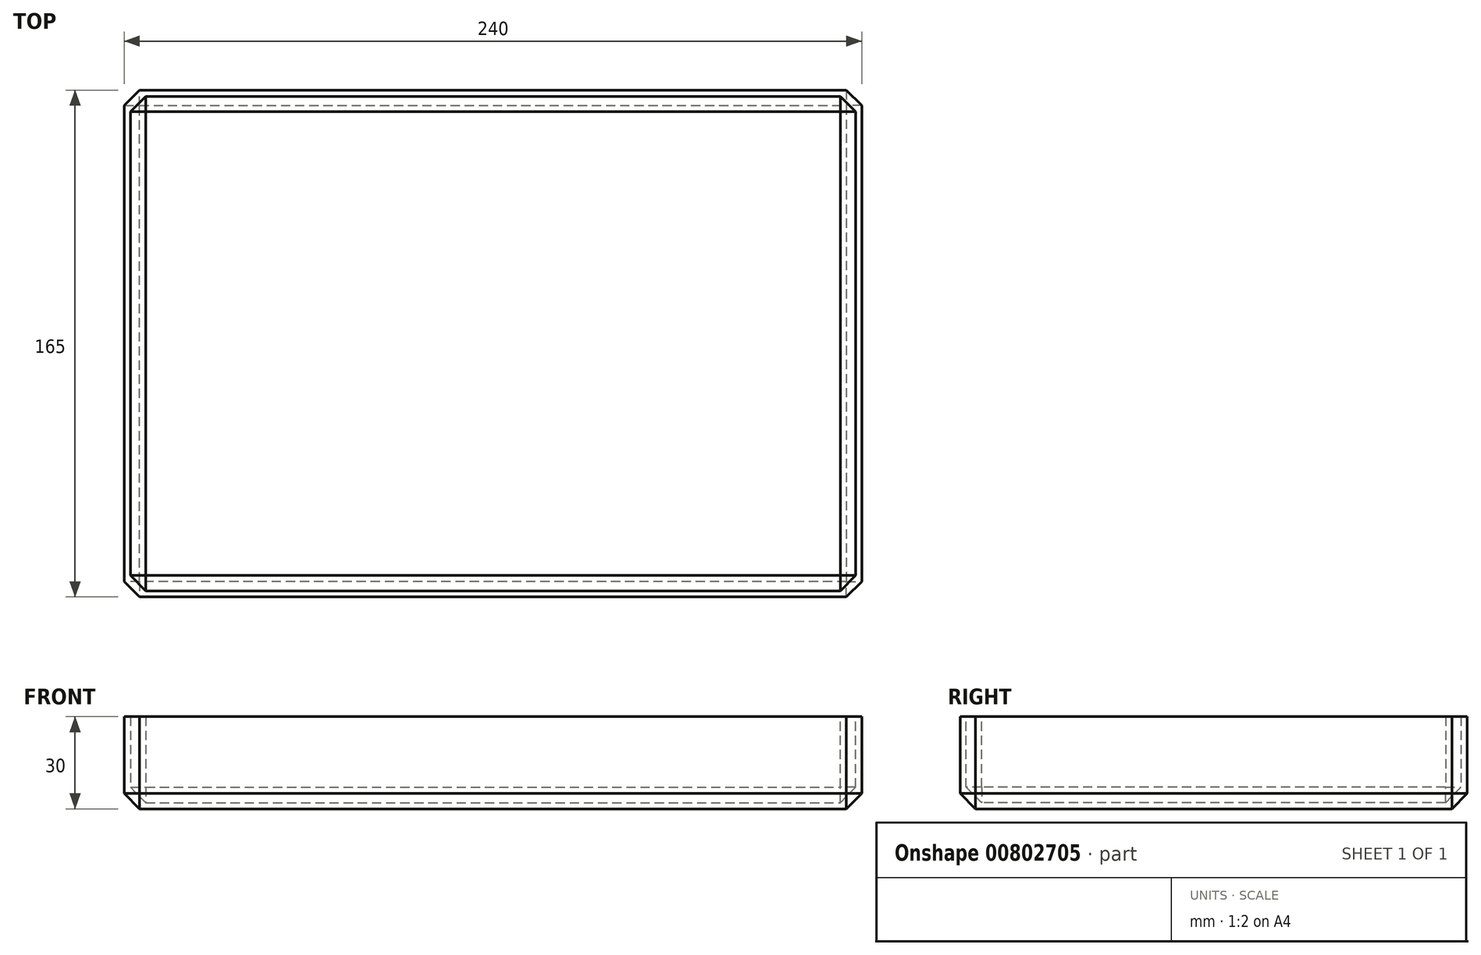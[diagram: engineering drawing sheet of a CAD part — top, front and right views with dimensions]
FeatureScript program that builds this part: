
annotation { "Feature Type Name" : "Feature", "Feature Type Description" : "" }
export const myFeature = defineFeature(function(context is Context, id is Id, definition is map)
    precondition{}
    {
        {
            var Q0;
            Q0=qCreatedBy(makeId("Top.planeOp"),FACE);
            var sketch = newSketch(context, id + "F0", { "sketchPlane" : qUnion([Q0])});
            skLineSegment(sketch, "E0.bottom", {"start": v(120, 82.5) * mm, "end": v(-120, 82.5) * mm});
            skLineSegment(sketch, "E0.top", {"start": v(120, -82.5) * mm, "end": v(-120, -82.5) * mm});
            skLineSegment(sketch, "E0.left", {"start": v(120, 82.5) * mm, "end": v(120, -82.5) * mm});
            skLineSegment(sketch, "E0.right", {"start": v(-120, 82.5) * mm, "end": v(-120, -82.5) * mm});
            skPoint(sketch, "E0.middle", {"position": v(0, 0) * mm});
            skSolve(sketch);
        }
        {
            var Q0;
            Q0 = qSketchRegion(id + "F0", true);
            extrude(context, id + "F1", {"entities" : qUnion([Q0]), "depth" : 30 * mm, "offsetDistance" : 25 * mm});
        }
        {
            var Q0;
            Q0=makeQuery(id+"F1.opExtrude","CAP_FACE",FACE,{"disambiguationData":[OSD([sQuery(id+"F0.wireOp",EDGE,"E0.bottom"),sQuery(id+"F0.wireOp",EDGE,"E0.top"),sQuery(id+"F0.wireOp",EDGE,"E0.left"),sQuery(id+"F0.wireOp",EDGE,"E0.right")])],"isStart":false});
            shell(context, id + "F2", {"entities" : qUnion([Q0]), "thickness" : 2 * mm});
        }
        {
            var Q0;
            Q0=makeQuery(id+"F2.opShell","OFFSET_EDGE",EDGE,{"disambiguationData":[OSD([sQuery(id+"F0.wireOp",EDGE,"E0.bottom"),sQuery(id+"F0.wireOp",EDGE,"E0.right")])]});
            var Q1;
            Q1=makeQuery(id+"F2.opShell","OFFSET_EDGE",EDGE,{"disambiguationData":[OSD([sQuery(id+"F0.wireOp",EDGE,"E0.bottom"),sQuery(id+"F0.wireOp",EDGE,"E0.left")])]});
            var Q2;
            Q2=makeQuery(id+"F2.opShell","OFFSET_EDGE",EDGE,{"disambiguationData":[OSD([sQuery(id+"F0.wireOp",EDGE,"E0.top"),sQuery(id+"F0.wireOp",EDGE,"E0.right")])]});
            var Q3;
            Q3=makeQuery(id+"F2.opShell","OFFSET_EDGE",EDGE,{"disambiguationData":[OSD([sQuery(id+"F0.wireOp",EDGE,"E0.top"),sQuery(id+"F0.wireOp",EDGE,"E0.left")])]});
            var Q4;
            Q4=makeQuery(id+"F1.opExtrude","SWEPT_EDGE",EDGE,{"disambiguationData":[OSD([sQuery(id+"F0.wireOp",EDGE,"E0.top"),sQuery(id+"F0.wireOp",EDGE,"E0.left")])]});
            var Q5;
            Q5=makeQuery(id+"F1.opExtrude","SWEPT_EDGE",EDGE,{"disambiguationData":[OSD([sQuery(id+"F0.wireOp",EDGE,"E0.bottom"),sQuery(id+"F0.wireOp",EDGE,"E0.left")])]});
            var Q6;
            Q6=makeQuery(id+"F1.opExtrude","SWEPT_EDGE",EDGE,{"disambiguationData":[OSD([sQuery(id+"F0.wireOp",EDGE,"E0.top"),sQuery(id+"F0.wireOp",EDGE,"E0.right")])]});
            var Q7;
            Q7=makeQuery(id+"F1.opExtrude","SWEPT_EDGE",EDGE,{"disambiguationData":[OSD([sQuery(id+"F0.wireOp",EDGE,"E0.bottom"),sQuery(id+"F0.wireOp",EDGE,"E0.right")])]});
            var Q8;
            Q8=makeQuery(id+"F1.opExtrude","CAP_FACE",FACE,{"disambiguationData":[OSD([sQuery(id+"F0.wireOp",EDGE,"E0.bottom"),sQuery(id+"F0.wireOp",EDGE,"E0.top"),sQuery(id+"F0.wireOp",EDGE,"E0.left"),sQuery(id+"F0.wireOp",EDGE,"E0.right")])],"isStart":true});
            var Q9;
            Q9=makeQuery(id+"F2.opShell","OFFSET_FACE",FACE,{"disambiguationData":[OSD([sQuery(id+"F0.wireOp",EDGE,"E0.bottom"),sQuery(id+"F0.wireOp",EDGE,"E0.top"),sQuery(id+"F0.wireOp",EDGE,"E0.left"),sQuery(id+"F0.wireOp",EDGE,"E0.right")])]});
            chamfer(context, id + "F3", {"entities" : qUnion([Q0, Q1, Q2, Q3, Q4, Q5, Q6, Q7, Q8, Q9]), "width" : 5 * mm, "tangentPropagation" : true});
        }
    });
